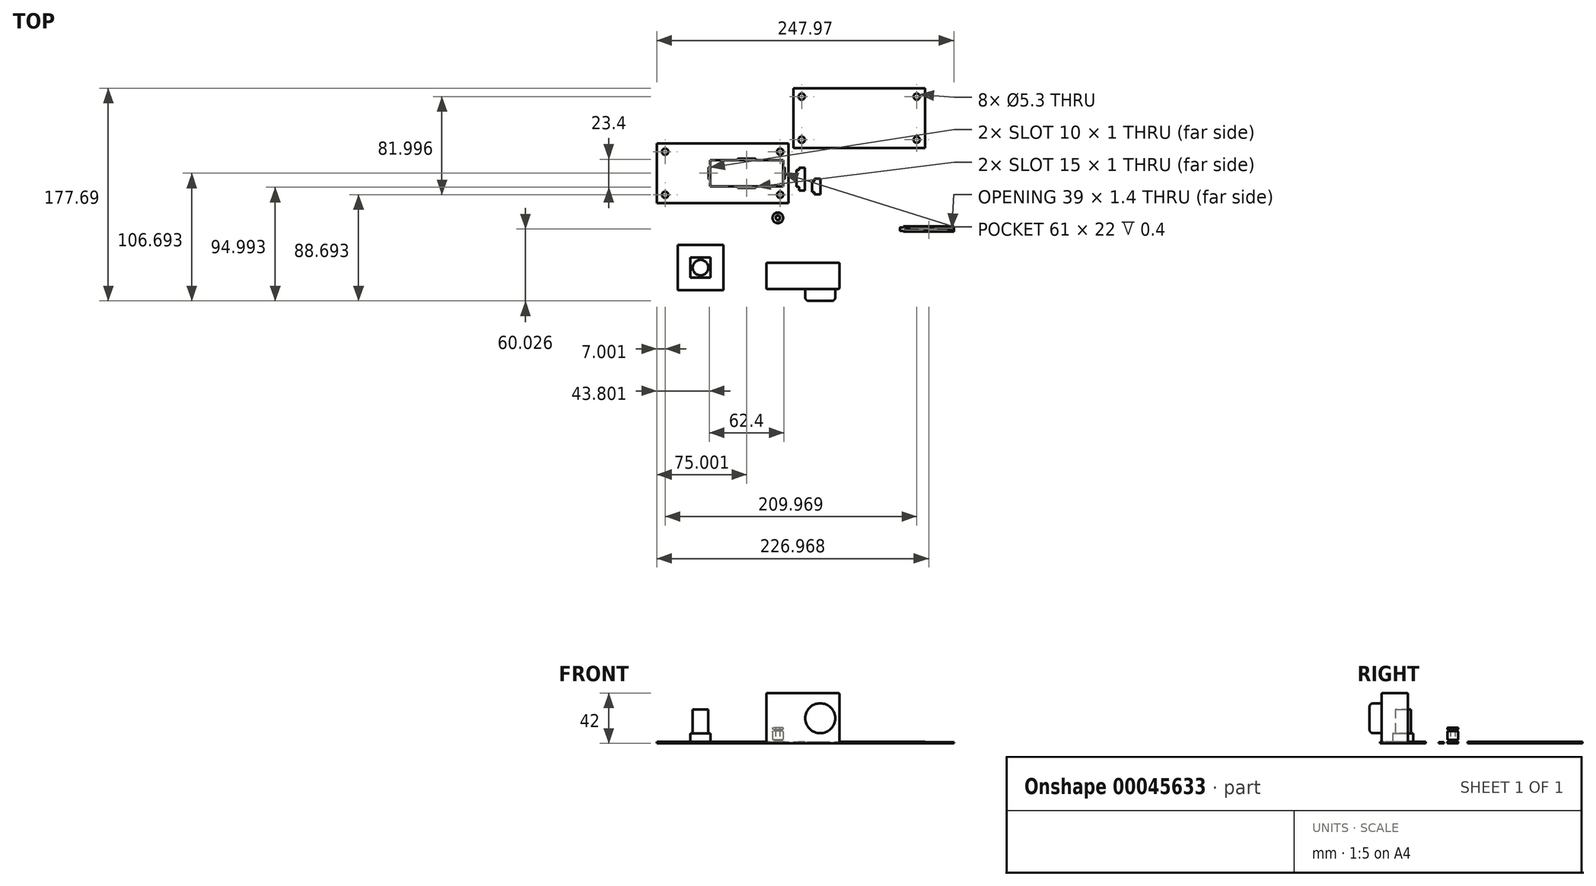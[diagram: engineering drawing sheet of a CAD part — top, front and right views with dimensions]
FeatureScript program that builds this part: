
annotation { "Feature Type Name" : "Feature", "Feature Type Description" : "" }
export const myFeature = defineFeature(function(context is Context, id is Id, definition is map)
    precondition{}
    {
        {
            var Q0;
            Q0=qCreatedBy(makeId("Top.planeOp"),FACE);
            var sketch = newSketch(context, id + "F0", { "sketchPlane" : qUnion([Q0])});
            skCircle(sketch, "E0", {"center": v(19.66, 8.56) * mm, "radius": 4.45 * mm});
            skCircle(sketch, "E1", {"center": v(19.66, 8.56) * mm, "radius": 1.75 * mm});
            skSolve(sketch);
        }
        {
            var Q0;
            Q0 = qSketchRegion(id + "F0", true);
            extrude(context, id + "F1", {"entities" : qUnion([Q0]), "depth" : 1.6 * mm});
        }
        {
            var Q0;
            Q0=makeQuery(id+"F1.opExtrude","CAP_FACE",FACE,{"disambiguationData":[OSD([sQuery(id+"F0.wireOp",EDGE,"E0"),sQuery(id+"F0.wireOp",EDGE,"E1")])],"isStart":false});
            var sketch = newSketch(context, id + "F2", { "sketchPlane" : qUnion([Q0])});
            skCircle(sketch, "E2", {"center": v(19.66, 8.56) * mm, "radius": 2.65 * mm});
            skCircle(sketch, "E3", {"center": v(19.66, 8.56) * mm, "radius": 1.75 * mm});
            skSolve(sketch);
        }
        {
            var Q0;
            Q0 = qSketchRegion(id + "F2", true);
            extrude(context, id + "F3", {"entities" : qUnion([Q0]), "operationType" : NewBodyOperationType.ADD, "depth" : 1.4 * mm});
        }
        {
            var Q0;
            Q0=makeQuery(id+"F3.opExtrude","CAP_FACE",FACE,{"disambiguationData":[OSD([sQuery(id+"F2.wireOp",EDGE,"E2"),sQuery(id+"F2.wireOp",EDGE,"E3")])],"isStart":false});
            var sketch = newSketch(context, id + "F4", { "sketchPlane" : qUnion([Q0])});
            skCircle(sketch, "E4", {"center": v(19.66, 8.56) * mm, "radius": 4.45 * mm});
            skCircle(sketch, "E5", {"center": v(19.66, 8.56) * mm, "radius": 1.75 * mm});
            skSolve(sketch);
        }
        {
            var Q0;
            Q0 = qSketchRegion(id + "F4", true);
            extrude(context, id + "F5", {"entities" : qUnion([Q0]), "operationType" : NewBodyOperationType.ADD, "depth" : 7.2 * mm});
        }
        {
            var Q0;
            Q0=makeQuery(id+"F5.opExtrude","CAP_FACE",FACE,{"disambiguationData":[OSD([sQuery(id+"F4.wireOp",EDGE,"E4"),sQuery(id+"F4.wireOp",EDGE,"E5")])],"isStart":false});
            var sketch = newSketch(context, id + "F6", { "sketchPlane" : qUnion([Q0])});
            skCircle(sketch, "E6", {"center": v(19.66, 8.56) * mm, "radius": 1.75 * mm});
            skCircle(sketch, "E7", {"center": v(19.66, 8.56) * mm, "radius": 2.65 * mm});
            skSolve(sketch);
        }
        {
            var Q0;
            Q0 = qSketchRegion(id + "F6", true);
            extrude(context, id + "F7", {"entities" : qUnion([Q0]), "operationType" : NewBodyOperationType.ADD, "depth" : 1.4 * mm});
        }
        {
            var Q0;
            Q0=makeQuery(id+"F7.opExtrude","CAP_FACE",FACE,{"disambiguationData":[OSD([sQuery(id+"F6.wireOp",EDGE,"E6"),sQuery(id+"F6.wireOp",EDGE,"E7")])],"isStart":false});
            var sketch = newSketch(context, id + "F8", { "sketchPlane" : qUnion([Q0])});
            skCircle(sketch, "E8", {"center": v(19.66, 8.56) * mm, "radius": 1.75 * mm});
            skCircle(sketch, "E9", {"center": v(19.66, 8.56) * mm, "radius": 4.45 * mm});
            skSolve(sketch);
        }
        {
            var Q0;
            Q0 = qSketchRegion(id + "F8", true);
            extrude(context, id + "F9", {"entities" : qUnion([Q0]), "operationType" : NewBodyOperationType.ADD, "depth" : 1.6 * mm});
        }
        {
            var Q0;
            Q0=makeQuery(id+"F9.opExtrude","CAP_EDGE",EDGE,{"disambiguationData":[OSD([sQuery(id+"F8.wireOp",EDGE,"E9")])],"isStart":false});
            var Q1;
            Q1=makeQuery(id+"F9.opExtrude","CAP_EDGE",EDGE,{"disambiguationData":[OSD([sQuery(id+"F8.wireOp",EDGE,"E9")])],"isStart":true});
            var Q2;
            Q2=makeQuery(id+"F5.opExtrude","CAP_EDGE",EDGE,{"disambiguationData":[OSD([sQuery(id+"F4.wireOp",EDGE,"E4")])],"isStart":false});
            var Q3;
            Q3=makeQuery(id+"F7.opExtrude","CAP_EDGE",EDGE,{"disambiguationData":[OSD([sQuery(id+"F6.wireOp",EDGE,"E7")])],"isStart":false});
            var Q4;
            Q4=makeQuery(id+"F7.opExtrude","CAP_EDGE",EDGE,{"disambiguationData":[OSD([sQuery(id+"F6.wireOp",EDGE,"E7")])],"isStart":true});
            var Q5;
            Q5=makeQuery(id+"F5.opExtrude","CAP_EDGE",EDGE,{"disambiguationData":[OSD([sQuery(id+"F4.wireOp",EDGE,"E4")])],"isStart":true});
            var Q6;
            Q6=makeQuery(id+"F3.opExtrude","CAP_EDGE",EDGE,{"disambiguationData":[OSD([sQuery(id+"F2.wireOp",EDGE,"E2")])],"isStart":false});
            var Q7;
            Q7=makeQuery(id+"F1.opExtrude","CAP_EDGE",EDGE,{"disambiguationData":[OSD([sQuery(id+"F0.wireOp",EDGE,"E0")])],"isStart":false});
            var Q8;
            Q8=makeQuery(id+"F1.opExtrude","CAP_EDGE",EDGE,{"disambiguationData":[OSD([sQuery(id+"F0.wireOp",EDGE,"E0")])],"isStart":true});
            var Q9;
            Q9=makeQuery(id+"F3.opExtrude","CAP_EDGE",EDGE,{"disambiguationData":[OSD([sQuery(id+"F2.wireOp",EDGE,"E2")])],"isStart":true});
            fillet(context, id + "F10", {"entities" : qUnion([Q0, Q1, Q2, Q3, Q4, Q5, Q6, Q7, Q8, Q9]), "radius" : 0.5 * mm, "tangentPropagation" : true, "allowEdgeOverflow" : false});
        }
        {
            var Q0;
            Q0=qCreatedBy(makeId("Top.planeOp"),FACE);
            var sketch = newSketch(context, id + "F11", { "sketchPlane" : qUnion([Q0])});
            skLineSegment(sketch, "E10.bottom", {"start": v(-81.37, 70.8) * mm, "end": v(28.63, 70.8) * mm});
            skLineSegment(sketch, "E10.top", {"start": v(-81.37, 20.8) * mm, "end": v(28.63, 20.8) * mm});
            skLineSegment(sketch, "E10.left", {"start": v(-81.37, 70.8) * mm, "end": v(-81.37, 20.8) * mm});
            skLineSegment(sketch, "E10.right", {"start": v(28.63, 70.8) * mm, "end": v(28.63, 20.8) * mm});
            skCircle(sketch, "E11", {"center": v(-74.37, 63.8) * mm, "radius": 2.65 * mm});
            skCircle(sketch, "E12", {"center": v(-74.37, 27.8) * mm, "radius": 2.65 * mm});
            skCircle(sketch, "E13", {"center": v(21.63, 63.8) * mm, "radius": 2.65 * mm});
            skCircle(sketch, "E14", {"center": v(21.63, 27.8) * mm, "radius": 2.65 * mm});
            skCircle(sketch, "E15", {"center": v(135.6, 73.8) * mm, "radius": 2.65 * mm});
            skCircle(sketch, "E16", {"center": v(39.6, 109.8) * mm, "radius": 2.65 * mm});
            skLineSegment(sketch, "E17.right", {"start": v(142.6, 116.8) * mm, "end": v(142.6, 66.8) * mm});
            skCircle(sketch, "E18", {"center": v(135.6, 109.8) * mm, "radius": 2.65 * mm});
            skCircle(sketch, "E19", {"center": v(39.6, 73.8) * mm, "radius": 2.65 * mm});
            skLineSegment(sketch, "E17.bottom", {"start": v(32.6, 116.8) * mm, "end": v(142.6, 116.8) * mm});
            skLineSegment(sketch, "E17.top", {"start": v(32.6, 66.8) * mm, "end": v(142.6, 66.8) * mm});
            skLineSegment(sketch, "E17.left", {"start": v(32.6, 116.8) * mm, "end": v(32.6, 66.8) * mm});
            skLineSegment(sketch, "E20.bottom", {"start": v(24.13, 56.8) * mm, "end": v(-36.87, 56.8) * mm});
            skLineSegment(sketch, "E20.top", {"start": v(24.13, 34.8) * mm, "end": v(-36.87, 34.8) * mm});
            skLineSegment(sketch, "E20.left", {"start": v(24.13, 56.8) * mm, "end": v(24.13, 34.8) * mm});
            skLineSegment(sketch, "E20.right", {"start": v(-36.87, 56.8) * mm, "end": v(-36.87, 34.8) * mm});
            skLineSegment(sketch, "E21", {"start": v(24.83, 50.8) * mm, "end": v(24.83, 50.8) * mm});
            skLineSegment(sketch, "E22", {"start": v(25.33, 50.3) * mm, "end": v(25.33, 41.3) * mm});
            skLineSegment(sketch, "E23", {"start": v(24.83, 40.8) * mm, "end": v(24.83, 40.8) * mm});
            skLineSegment(sketch, "E24", {"start": v(24.33, 41.3) * mm, "end": v(24.33, 50.3) * mm});
            skPoint(sketch, "E25.visualSharp", {"position": v(24.33, 50.8) * mm});
            skArc(sketch, "E25.filletArc", {"start": v(24.83, 50.8) * mm, "mid": v(24.48, 50.66) * mm, "end": v(24.33, 50.3) * mm});
            skPoint(sketch, "E26.visualSharp", {"position": v(25.33, 50.8) * mm});
            skArc(sketch, "E26.filletArc", {"start": v(25.33, 50.3) * mm, "mid": v(25.18, 50.66) * mm, "end": v(24.83, 50.8) * mm});
            skPoint(sketch, "E27.visualSharp", {"position": v(24.33, 40.8) * mm});
            skArc(sketch, "E27.filletArc", {"start": v(24.33, 41.3) * mm, "mid": v(24.48, 40.95) * mm, "end": v(24.83, 40.8) * mm});
            skPoint(sketch, "E28.visualSharp", {"position": v(25.33, 40.8) * mm});
            skArc(sketch, "E28.filletArc", {"start": v(24.83, 40.8) * mm, "mid": v(25.18, 40.95) * mm, "end": v(25.33, 41.3) * mm});
            skLineSegment(sketch, "E29", {"start": v(-6.37, 56.8) * mm, "end": v(-6.37, 34.8) * mm});
            skLineSegment(sketch, "E30.MirrorCS", {"start": v(-37.07, 41.3) * mm, "end": v(-37.07, 50.3) * mm});
            skArc(sketch, "E31.MirrorCS", {"start": v(-37.57, 50.8) * mm, "mid": v(-37.22, 50.66) * mm, "end": v(-37.07, 50.3) * mm});
            skLineSegment(sketch, "E32.MirrorCS", {"start": v(-37.57, 50.8) * mm, "end": v(-37.57, 50.8) * mm});
            skArc(sketch, "E33.MirrorCS", {"start": v(-38.07, 50.3) * mm, "mid": v(-37.92, 50.66) * mm, "end": v(-37.57, 50.8) * mm});
            skLineSegment(sketch, "E34.MirrorCS", {"start": v(-38.07, 50.3) * mm, "end": v(-38.07, 41.3) * mm});
            skArc(sketch, "E35.MirrorCS", {"start": v(-37.57, 40.8) * mm, "mid": v(-37.92, 40.95) * mm, "end": v(-38.07, 41.3) * mm});
            skLineSegment(sketch, "E36.MirrorCS", {"start": v(-37.57, 40.8) * mm, "end": v(-37.57, 40.8) * mm});
            skArc(sketch, "E37.MirrorCS", {"start": v(-37.07, 41.3) * mm, "mid": v(-37.22, 40.95) * mm, "end": v(-37.57, 40.8) * mm});
            skLineSegment(sketch, "E38", {"start": v(-13.37, 57) * mm, "end": v(0.63, 57) * mm});
            skLineSegment(sketch, "E39", {"start": v(1.13, 57.5) * mm, "end": v(1.13, 57.5) * mm});
            skLineSegment(sketch, "E40", {"start": v(0.63, 58) * mm, "end": v(-13.37, 58) * mm});
            skLineSegment(sketch, "E41", {"start": v(-13.87, 57.5) * mm, "end": v(-13.87, 57.5) * mm});
            skLineSegment(sketch, "E42", {"start": v(-36.87, 45.8) * mm, "end": v(24.13, 45.8) * mm});
            skPoint(sketch, "E43.visualSharp", {"position": v(1.13, 58) * mm});
            skArc(sketch, "E43.filletArc", {"start": v(1.13, 57.5) * mm, "mid": v(0.98, 57.86) * mm, "end": v(0.63, 58) * mm});
            skPoint(sketch, "E44.visualSharp", {"position": v(1.13, 57) * mm});
            skArc(sketch, "E44.filletArc", {"start": v(0.63, 57) * mm, "mid": v(0.98, 57.15) * mm, "end": v(1.13, 57.5) * mm});
            skPoint(sketch, "E45.visualSharp", {"position": v(-13.87, 58) * mm});
            skArc(sketch, "E45.filletArc", {"start": v(-13.37, 58) * mm, "mid": v(-13.72, 57.86) * mm, "end": v(-13.87, 57.5) * mm});
            skPoint(sketch, "E46.visualSharp", {"position": v(-13.87, 57) * mm});
            skArc(sketch, "E46.filletArc", {"start": v(-13.87, 57.5) * mm, "mid": v(-13.72, 57.15) * mm, "end": v(-13.37, 57) * mm});
            skLineSegment(sketch, "E47.MirrorCS", {"start": v(-13.87, 34.1) * mm, "end": v(-13.87, 34.1) * mm});
            skArc(sketch, "E48.MirrorCS", {"start": v(-13.37, 33.6) * mm, "mid": v(-13.72, 33.75) * mm, "end": v(-13.87, 34.1) * mm});
            skLineSegment(sketch, "E49.MirrorCS", {"start": v(0.63, 33.6) * mm, "end": v(-13.37, 33.6) * mm});
            skArc(sketch, "E50.MirrorCS", {"start": v(-13.87, 34.1) * mm, "mid": v(-13.72, 34.46) * mm, "end": v(-13.37, 34.6) * mm});
            skLineSegment(sketch, "E51.MirrorCS", {"start": v(-13.37, 34.6) * mm, "end": v(0.63, 34.6) * mm});
            skArc(sketch, "E52.MirrorCS", {"start": v(1.13, 34.1) * mm, "mid": v(0.98, 33.75) * mm, "end": v(0.63, 33.6) * mm});
            skLineSegment(sketch, "E53.MirrorCS", {"start": v(1.13, 34.1) * mm, "end": v(1.13, 34.1) * mm});
            skArc(sketch, "E54.MirrorCS", {"start": v(0.63, 34.6) * mm, "mid": v(0.98, 34.46) * mm, "end": v(1.13, 34.1) * mm});
            skLineSegment(sketch, "E55", {"start": v(48.25, 39.1) * mm, "end": v(49.75, 39.1) * mm});
            skLineSegment(sketch, "E56", {"start": v(50.25, 39.6) * mm, "end": v(50.25, 41.1) * mm});
            skLineSegment(sketch, "E57", {"start": v(50.25, 41.1) * mm, "end": v(55.25, 41.1) * mm});
            skLineSegment(sketch, "E58", {"start": v(55.25, 41.1) * mm, "end": v(55.25, 28.1) * mm});
            skLineSegment(sketch, "E59", {"start": v(55.25, 28.1) * mm, "end": v(50.25, 28.1) * mm});
            skLineSegment(sketch, "E60", {"start": v(50.25, 28.1) * mm, "end": v(50.25, 29.6) * mm});
            skLineSegment(sketch, "E61", {"start": v(49.75, 30.1) * mm, "end": v(48.25, 30.1) * mm});
            skLineSegment(sketch, "E62", {"start": v(48.25, 30.1) * mm, "end": v(48.25, 39.1) * mm});
            skLineSegment(sketch, "E63", {"start": v(35.35, 48.45) * mm, "end": v(36.85, 48.45) * mm});
            skLineSegment(sketch, "E64", {"start": v(37.35, 48.95) * mm, "end": v(37.35, 50.45) * mm});
            skLineSegment(sketch, "E65", {"start": v(37.35, 50.45) * mm, "end": v(42.35, 50.45) * mm});
            skLineSegment(sketch, "E66", {"start": v(42.35, 50.45) * mm, "end": v(42.35, 31.18) * mm});
            skLineSegment(sketch, "E67", {"start": v(42.35, 31.18) * mm, "end": v(37.35, 31.18) * mm});
            skLineSegment(sketch, "E68", {"start": v(37.35, 31.18) * mm, "end": v(37.35, 33.95) * mm});
            skLineSegment(sketch, "E69", {"start": v(36.85, 34.45) * mm, "end": v(35.35, 34.45) * mm});
            skLineSegment(sketch, "E70", {"start": v(35.35, 34.45) * mm, "end": v(35.35, 48.45) * mm});
            skPoint(sketch, "E71.visualSharp", {"position": v(37.35, 48.45) * mm});
            skArc(sketch, "E71.filletArc", {"start": v(36.85, 48.45) * mm, "mid": v(37.2, 48.6) * mm, "end": v(37.35, 48.95) * mm});
            skPoint(sketch, "E72.visualSharp", {"position": v(37.35, 34.45) * mm});
            skArc(sketch, "E72.filletArc", {"start": v(37.35, 33.95) * mm, "mid": v(37.2, 34.3) * mm, "end": v(36.85, 34.45) * mm});
            skPoint(sketch, "E73.visualSharp", {"position": v(50.25, 30.1) * mm});
            skArc(sketch, "E73.filletArc", {"start": v(50.25, 29.6) * mm, "mid": v(50.1, 29.96) * mm, "end": v(49.75, 30.1) * mm});
            skPoint(sketch, "E74.visualSharp", {"position": v(50.25, 39.1) * mm});
            skArc(sketch, "E74.filletArc", {"start": v(49.75, 39.1) * mm, "mid": v(50.1, 39.26) * mm, "end": v(50.25, 39.6) * mm});
            skSolve(sketch);
        }
        {
            var Q0;
            Q0=makeQuery(id+"F11.imprint","IMPRINT",FACE,{"disambiguationData":[TD([[makeQuery(id+"F11.imprint","IMPRINT",EDGE,{"derivedFrom":sQuery(id+"F11.wireOp",EDGE,"E10.bottom")}),-1.0]])]});
            var Q1;
            {var subQ0=sQuery(id+"F11.wireOp",EDGE,"E20.right");var subQ1=sQuery(id+"F11.wireOp",EDGE,"E20.bottom");var subQ2=makeQuery(id+"F11.imprint","INTERSECT",VERTEX,{"derivedFrom":[subQ1,subQ0]});Q1=makeQuery(id+"F11.imprint","IMPRINT",FACE,{"disambiguationData":[TD([[makeQuery(id+"F11.imprint","IMPRINT",EDGE,{"disambiguationData":[TD([[subQ2,1.0]])],"derivedFrom":subQ1}),1.0]])]});}
            var Q2;
            {var subQ0=sQuery(id+"F11.wireOp",EDGE,"E20.right");var subQ1=sQuery(id+"F11.wireOp",EDGE,"E20.top");var subQ2=makeQuery(id+"F11.imprint","INTERSECT",VERTEX,{"derivedFrom":[subQ1,subQ0]});Q2=makeQuery(id+"F11.imprint","IMPRINT",FACE,{"disambiguationData":[TD([[makeQuery(id+"F11.imprint","IMPRINT",EDGE,{"disambiguationData":[TD([[subQ2,1.0]])],"derivedFrom":subQ1}),-1.0]])]});}
            var Q3;
            {var subQ0=sQuery(id+"F11.wireOp",EDGE,"E20.left");var subQ1=sQuery(id+"F11.wireOp",EDGE,"E20.top");var subQ2=makeQuery(id+"F11.imprint","INTERSECT",VERTEX,{"derivedFrom":[subQ1,subQ0]});Q3=makeQuery(id+"F11.imprint","IMPRINT",FACE,{"disambiguationData":[TD([[makeQuery(id+"F11.imprint","IMPRINT",EDGE,{"disambiguationData":[TD([[subQ2,-1.0]])],"derivedFrom":subQ1}),-1.0]])]});}
            var Q4;
            {var subQ0=sQuery(id+"F11.wireOp",EDGE,"E20.left");var subQ1=sQuery(id+"F11.wireOp",EDGE,"E20.bottom");var subQ2=makeQuery(id+"F11.imprint","INTERSECT",VERTEX,{"derivedFrom":[subQ1,subQ0]});Q4=makeQuery(id+"F11.imprint","IMPRINT",FACE,{"disambiguationData":[TD([[makeQuery(id+"F11.imprint","IMPRINT",EDGE,{"disambiguationData":[TD([[subQ2,-1.0]])],"derivedFrom":subQ1}),1.0]])]});}
            var Q5;
            Q5=makeQuery(id+"F11.imprint","IMPRINT",FACE,{"disambiguationData":[TD([[makeQuery(id+"F11.imprint","IMPRINT",EDGE,{"derivedFrom":sQuery(id+"F11.wireOp",EDGE,"E63")}),-1.0]])]});
            var Q6;
            Q6=makeQuery(id+"F11.imprint","IMPRINT",FACE,{"disambiguationData":[TD([[makeQuery(id+"F11.imprint","IMPRINT",EDGE,{"derivedFrom":sQuery(id+"F11.wireOp",EDGE,"E55")}),-1.0]])]});
            extrude(context, id + "F12", {"entities" : qUnion([Q0, Q1, Q2, Q3, Q4, Q5, Q6]), "depth" : 1 * mm});
        }
        {
            var Q0;
            Q0 = qSketchRegion(id + "F11", true);
            extrude(context, id + "F13", {"entities" : qUnion([Q0]), "operationType" : NewBodyOperationType.ADD, "depth" : 1.4 * mm});
        }
        {
            var Q0;
            Q0=qCreatedBy(makeId("Top.planeOp"),FACE);
            var sketch = newSketch(context, id + "F14", { "sketchPlane" : qUnion([Q0])});
            skLineSegment(sketch, "E75.bottom", {"start": v(10.1, -28.9) * mm, "end": v(71.1, -28.9) * mm});
            skLineSegment(sketch, "E75.top", {"start": v(10.1, -50.9) * mm, "end": v(71.1, -50.9) * mm});
            skLineSegment(sketch, "E75.left", {"start": v(10.1, -28.9) * mm, "end": v(10.1, -50.9) * mm});
            skLineSegment(sketch, "E75.right", {"start": v(71.1, -28.9) * mm, "end": v(71.1, -50.9) * mm});
            skSolve(sketch);
        }
        {
            var Q0;
            Q0 = qSketchRegion(id + "F14", true);
            extrude(context, id + "F15", {"entities" : qUnion([Q0]), "depth" : 42 * mm});
        }
        {
            var Q0;
            Q0=makeQuery(id+"F15.opExtrude","SWEPT_FACE",FACE,{"disambiguationData":[OSD([sQuery(id+"F14.wireOp",EDGE,"E75.top")])]});
            var sketch = newSketch(context, id + "F16", { "sketchPlane" : qUnion([Q0])});
            skCircle(sketch, "E76", {"center": v(55.1, 21) * mm, "radius": 12.5 * mm});
            skSolve(sketch);
        }
        {
            var Q0;
            Q0 = qSketchRegion(id + "F16", true);
            extrude(context, id + "F17", {"entities" : qUnion([Q0]), "operationType" : NewBodyOperationType.ADD, "depth" : 10 * mm});
        }
        {
            var Q0;
            Q0=makeQuery(id+"F17.opExtrude","CAP_EDGE",EDGE,{"disambiguationData":[OSD([sQuery(id+"F16.wireOp",EDGE,"E76")])],"isStart":false});
            fillet(context, id + "F18", {"entities" : qUnion([Q0]), "radius" : 3 * mm, "tangentPropagation" : true, "allowEdgeOverflow" : false});
        }
        {
            var Q0;
            Q0=makeQuery(id+"F15.opExtrude","CAP_EDGE",EDGE,{"disambiguationData":[OSD([sQuery(id+"F14.wireOp",EDGE,"E75.top")])],"isStart":false});
            var Q1;
            Q1=makeQuery(id+"F15.opExtrude","CAP_EDGE",EDGE,{"disambiguationData":[OSD([sQuery(id+"F14.wireOp",EDGE,"E75.right")])],"isStart":false});
            var Q2;
            Q2=makeQuery(id+"F15.opExtrude","SWEPT_EDGE",EDGE,{"disambiguationData":[OSD([sQuery(id+"F14.wireOp",EDGE,"E75.top"),sQuery(id+"F14.wireOp",EDGE,"E75.right")])]});
            var Q3;
            Q3=makeQuery(id+"F15.opExtrude","SWEPT_EDGE",EDGE,{"disambiguationData":[OSD([sQuery(id+"F14.wireOp",EDGE,"E75.bottom"),sQuery(id+"F14.wireOp",EDGE,"E75.right")])]});
            var Q4;
            Q4=makeQuery(id+"F15.opExtrude","CAP_EDGE",EDGE,{"disambiguationData":[OSD([sQuery(id+"F14.wireOp",EDGE,"E75.bottom")])],"isStart":false});
            var Q5;
            Q5=makeQuery(id+"F15.opExtrude","CAP_EDGE",EDGE,{"disambiguationData":[OSD([sQuery(id+"F14.wireOp",EDGE,"E75.left")])],"isStart":false});
            var Q6;
            Q6=makeQuery(id+"F15.opExtrude","SWEPT_EDGE",EDGE,{"disambiguationData":[OSD([sQuery(id+"F14.wireOp",EDGE,"E75.top"),sQuery(id+"F14.wireOp",EDGE,"E75.left")])]});
            var Q7;
            Q7=makeQuery(id+"F15.opExtrude","CAP_EDGE",EDGE,{"disambiguationData":[OSD([sQuery(id+"F14.wireOp",EDGE,"E75.top")])],"isStart":true});
            var Q8;
            Q8=makeQuery(id+"F15.opExtrude","SWEPT_EDGE",EDGE,{"disambiguationData":[OSD([sQuery(id+"F14.wireOp",EDGE,"E75.bottom"),sQuery(id+"F14.wireOp",EDGE,"E75.left")])]});
            var Q9;
            Q9=makeQuery(id+"F15.opExtrude","CAP_EDGE",EDGE,{"disambiguationData":[OSD([sQuery(id+"F14.wireOp",EDGE,"E75.bottom")])],"isStart":true});
            var Q10;
            Q10=makeQuery(id+"F15.opExtrude","CAP_EDGE",EDGE,{"disambiguationData":[OSD([sQuery(id+"F14.wireOp",EDGE,"E75.left")])],"isStart":true});
            fillet(context, id + "F19", {"entities" : qUnion([Q0, Q1, Q2, Q3, Q4, Q5, Q6, Q7, Q8, Q9, Q10]), "radius" : 1 * mm, "tangentPropagation" : true, "allowEdgeOverflow" : false});
        }
        {
            var Q0;
            Q0=qCreatedBy(makeId("Top.planeOp"),FACE);
            var sketch = newSketch(context, id + "F20", { "sketchPlane" : qUnion([Q0])});
            skLineSegment(sketch, "E77.bottom", {"start": v(-63.87, -14) * mm, "end": v(-25.87, -14) * mm});
            skLineSegment(sketch, "E77.top", {"start": v(-63.87, -52) * mm, "end": v(-25.87, -52) * mm});
            skLineSegment(sketch, "E77.left", {"start": v(-63.87, -14) * mm, "end": v(-63.87, -52) * mm});
            skLineSegment(sketch, "E77.right", {"start": v(-25.87, -14) * mm, "end": v(-25.87, -52) * mm});
            skSolve(sketch);
        }
        {
            var Q0;
            Q0 = qSketchRegion(id + "F20", true);
            extrude(context, id + "F21", {"entities" : qUnion([Q0]), "depth" : 1.4 * mm});
        }
        {
            var Q0;
            Q0=makeQuery(id+"F21.opExtrude","CAP_FACE",FACE,{"disambiguationData":[OSD([sQuery(id+"F20.wireOp",EDGE,"E77.bottom"),sQuery(id+"F20.wireOp",EDGE,"E77.top"),sQuery(id+"F20.wireOp",EDGE,"E77.left"),sQuery(id+"F20.wireOp",EDGE,"E77.right")])],"isStart":false});
            var sketch = newSketch(context, id + "F22", { "sketchPlane" : qUnion([Q0])});
            skLineSegment(sketch, "E78", {"start": v(-53.37, -24.5) * mm, "end": v(-36.37, -24.5) * mm});
            skLineSegment(sketch, "E79", {"start": v(-36.37, -24.5) * mm, "end": v(-36.37, -41.5) * mm});
            skLineSegment(sketch, "E80", {"start": v(-36.37, -41.5) * mm, "end": v(-53.37, -41.5) * mm});
            skLineSegment(sketch, "E81", {"start": v(-53.37, -41.5) * mm, "end": v(-53.37, -24.5) * mm});
            skSolve(sketch);
        }
        {
            var Q0;
            Q0 = qSketchRegion(id + "F22", true);
            extrude(context, id + "F23", {"entities" : qUnion([Q0]), "operationType" : NewBodyOperationType.ADD, "depth" : 7 * mm});
        }
        {
            var Q0;
            Q0=makeQuery(id+"F23.opExtrude","CAP_FACE",FACE,{"disambiguationData":[OSD([sQuery(id+"F22.wireOp",EDGE,"E78"),sQuery(id+"F22.wireOp",EDGE,"E79"),sQuery(id+"F22.wireOp",EDGE,"E80"),sQuery(id+"F22.wireOp",EDGE,"E81")])],"isStart":false});
            var sketch = newSketch(context, id + "F24", { "sketchPlane" : qUnion([Q0])});
            skLineSegment(sketch, "E82", {"start": v(-53.37, -24.5) * mm, "end": v(-36.37, -41.5) * mm});
            skLineSegment(sketch, "E83", {"start": v(-53.37, -41.5) * mm, "end": v(-36.37, -24.5) * mm});
            skPoint(sketch, "E84", {"position": v(-44.87, -33) * mm});
            skCircle(sketch, "E85", {"center": v(-44.87, -33) * mm, "radius": 6.5 * mm});
            skSolve(sketch);
        }
        {
            var Q0;
            Q0 = qSketchRegion(id + "F24", true);
            extrude(context, id + "F25", {"entities" : qUnion([Q0]), "operationType" : NewBodyOperationType.ADD, "depth" : 20 * mm});
        }
        {
            var Q0;
            Q0=qCreatedBy(makeId("Top.planeOp"),FACE);
            var sketch = newSketch(context, id + "F26", { "sketchPlane" : qUnion([Q0])});
            skLineSegment(sketch, "E86.bottom", {"start": v(126.6, -0.16) * mm, "end": v(164.6, -0.16) * mm});
            skLineSegment(sketch, "E86.top", {"start": v(126.6, -1.56) * mm, "end": v(164.6, -1.56) * mm});
            skLineSegment(sketch, "E86.left", {"start": v(126.1, -0.66) * mm, "end": v(126.1, -1.06) * mm});
            skLineSegment(sketch, "E86.right", {"start": v(165.1, -0.66) * mm, "end": v(165.1, -1.06) * mm});
            skLineSegment(sketch, "E87.bottom", {"start": v(166.6, 1.34) * mm, "end": v(124.6, 1.34) * mm});
            skLineSegment(sketch, "E87.top", {"start": v(166.6, -3.06) * mm, "end": v(124.6, -3.06) * mm});
            skLineSegment(sketch, "E87.left", {"start": v(166.6, 1.34) * mm, "end": v(166.6, -3.06) * mm});
            skLineSegment(sketch, "E87.right", {"start": v(124.6, 1.34) * mm, "end": v(124.6, 1.14) * mm});
            skPoint(sketch, "E88.visualSharp", {"position": v(126.1, -0.16) * mm});
            skArc(sketch, "E88.filletArc", {"start": v(126.6, -0.16) * mm, "mid": v(126.24, -0.31) * mm, "end": v(126.1, -0.66) * mm});
            skPoint(sketch, "E89.visualSharp", {"position": v(126.1, -1.56) * mm});
            skArc(sketch, "E89.filletArc", {"start": v(126.1, -1.06) * mm, "mid": v(126.24, -1.42) * mm, "end": v(126.6, -1.56) * mm});
            skPoint(sketch, "E90.visualSharp", {"position": v(165.1, -1.56) * mm});
            skArc(sketch, "E90.filletArc", {"start": v(164.6, -1.56) * mm, "mid": v(164.95, -1.42) * mm, "end": v(165.1, -1.06) * mm});
            skPoint(sketch, "E91.visualSharp", {"position": v(165.1, -0.16) * mm});
            skArc(sketch, "E91.filletArc", {"start": v(165.1, -0.66) * mm, "mid": v(164.95, -0.31) * mm, "end": v(164.6, -0.16) * mm});
            skLineSegment(sketch, "E92", {"start": v(124.1, 0.64) * mm, "end": v(122.1, 0.64) * mm});
            skLineSegment(sketch, "E93", {"start": v(121.6, 0.14) * mm, "end": v(121.6, -1.86) * mm});
            skLineSegment(sketch, "E94", {"start": v(122.1, -2.36) * mm, "end": v(124.1, -2.36) * mm});
            skArc(sketch, "E95.filletArc", {"start": v(124.1, 0.64) * mm, "mid": v(124.45, 0.78) * mm, "end": v(124.6, 1.14) * mm});
            skLineSegment(sketch, "E96", {"start": v(124.6, -2.86) * mm, "end": v(124.6, -3.06) * mm});
            skPoint(sketch, "E97.visualSharp", {"position": v(124.6, -2.36) * mm});
            skArc(sketch, "E97.filletArc", {"start": v(124.6, -2.86) * mm, "mid": v(124.45, -2.51) * mm, "end": v(124.1, -2.36) * mm});
            skPoint(sketch, "E98.visualSharp", {"position": v(121.6, 0.64) * mm});
            skArc(sketch, "E98.filletArc", {"start": v(122.1, 0.64) * mm, "mid": v(121.74, 0.49) * mm, "end": v(121.6, 0.14) * mm});
            skPoint(sketch, "E99.visualSharp", {"position": v(121.6, -2.36) * mm});
            skArc(sketch, "E99.filletArc", {"start": v(121.6, -1.86) * mm, "mid": v(121.74, -2.22) * mm, "end": v(122.1, -2.36) * mm});
            skSolve(sketch);
        }
        {
            var Q0;
            Q0=makeQuery(id+"F26.imprint","IMPRINT",FACE,{"disambiguationData":[TD([[makeQuery(id+"F26.imprint","IMPRINT",EDGE,{"derivedFrom":sQuery(id+"F26.wireOp",EDGE,"E86.bottom")}),1.0]])]});
            extrude(context, id + "F27", {"entities" : qUnion([Q0]), "depth" : 1 * mm});
        }
    });
